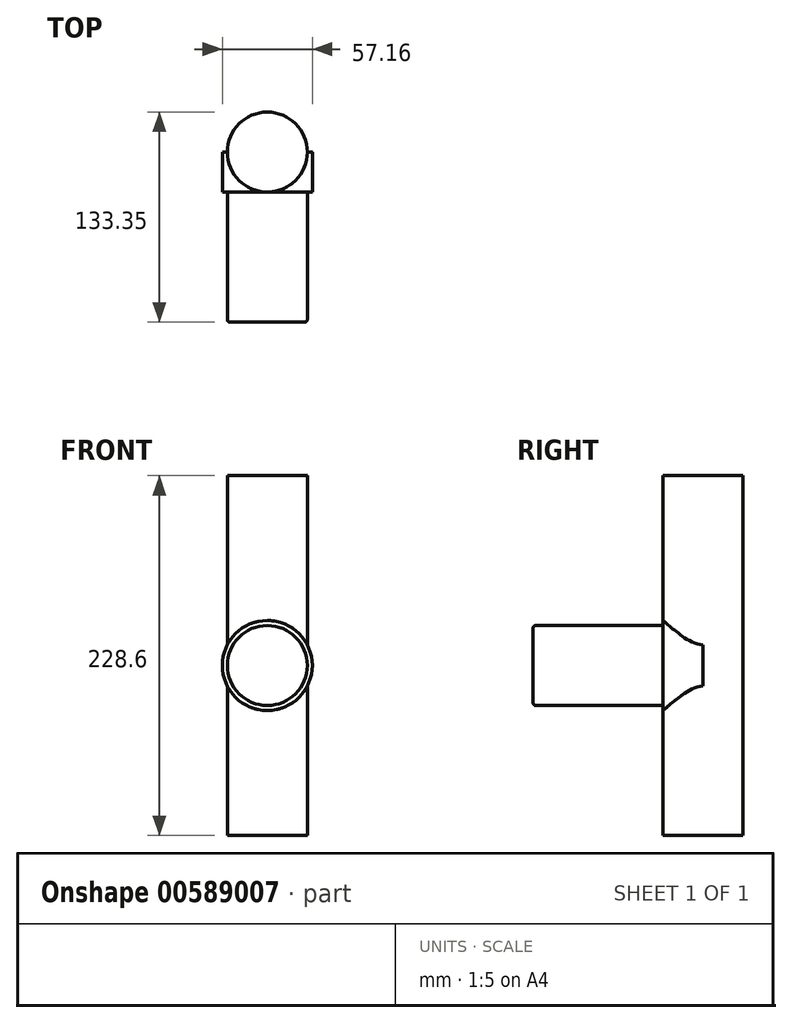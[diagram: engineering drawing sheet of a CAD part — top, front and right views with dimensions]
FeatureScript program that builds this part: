
annotation { "Feature Type Name" : "Feature", "Feature Type Description" : "" }
export const myFeature = defineFeature(function(context is Context, id is Id, definition is map)
    precondition{}
    {
        {
            var Q0;
            Q0=qCreatedBy(makeId("Front.planeOp"),FACE);
            var sketch = newSketch(context, id + "F0", { "sketchPlane" : qUnion([Q0])});
            skCircle(sketch, "E0", {"center": v(0, 0) * mm, "radius": 28.58 * mm});
            skSolve(sketch);
        }
        {
            var Q0;
            Q0 = qSketchRegion(id + "F0", true);
            extrude(context, id + "F1", {"entities" : qUnion([Q0]), "depth" : 25.4 * mm, "offsetDistance" : 25.4 * mm});
        }
        {
            var Q0;
            Q0=makeQuery(id+"F1.opExtrude","CAP_FACE",FACE,{"disambiguationData":[OSD([sQuery(id+"F0.wireOp",EDGE,"E0")])],"isStart":false});
            var sketch = newSketch(context, id + "F2", { "sketchPlane" : qUnion([Q0])});
            skCircle(sketch, "E1", {"center": v(0, 0) * mm, "radius": 25.4 * mm});
            skSolve(sketch);
        }
        {
            var Q0;
            Q0 = qSketchRegion(id + "F2", true);
            extrude(context, id + "F3", {"entities" : qUnion([Q0]), "operationType" : NewBodyOperationType.ADD, "depth" : 82.55 * mm, "offsetDistance" : 25.4 * mm});
        }
        {
            var Q0;
            Q0=qCreatedBy(makeId("Top.planeOp"),FACE);
            var sketch = newSketch(context, id + "F4", { "sketchPlane" : qUnion([Q0])});
            skCircle(sketch, "E2", {"center": v(0, 0) * mm, "radius": 25.4 * mm});
            skSolve(sketch);
        }
        {
            var Q0;
            Q0 = qSketchRegion(id + "F4", true);
            extrude(context, id + "F5", {"entities" : qUnion([Q0]), "operationType" : NewBodyOperationType.ADD, "oppositeDirection" : true, "depth" : 107.95 * mm, "offsetDistance" : 25.4 * mm});
        }
        {
            var Q0;
            Q0=qCreatedBy(makeId("Top.planeOp"),FACE);
            var sketch = newSketch(context, id + "F6", { "sketchPlane" : qUnion([Q0])});
            skCircle(sketch, "E3", {"center": v(0, 0) * mm, "radius": 25.4 * mm});
            skSolve(sketch);
        }
        {
            var Q0;
            Q0 = qSketchRegion(id + "F6", true);
            extrude(context, id + "F7", {"entities" : qUnion([Q0]), "operationType" : NewBodyOperationType.ADD, "depth" : 120.65 * mm, "offsetDistance" : 25.4 * mm});
        }
        {
            var Q0;
            Q0=makeQuery(id+"F3.opExtrude","CAP_FACE",FACE,{"disambiguationData":[OSD([sQuery(id+"F2.wireOp",EDGE,"E1")])],"isStart":false});
            fillet(context, id + "F8", {"entities" : qUnion([Q0]), "radius" : 1.59 * mm, "tangentPropagation" : true, "allowEdgeOverflow" : false});
        }
    });
